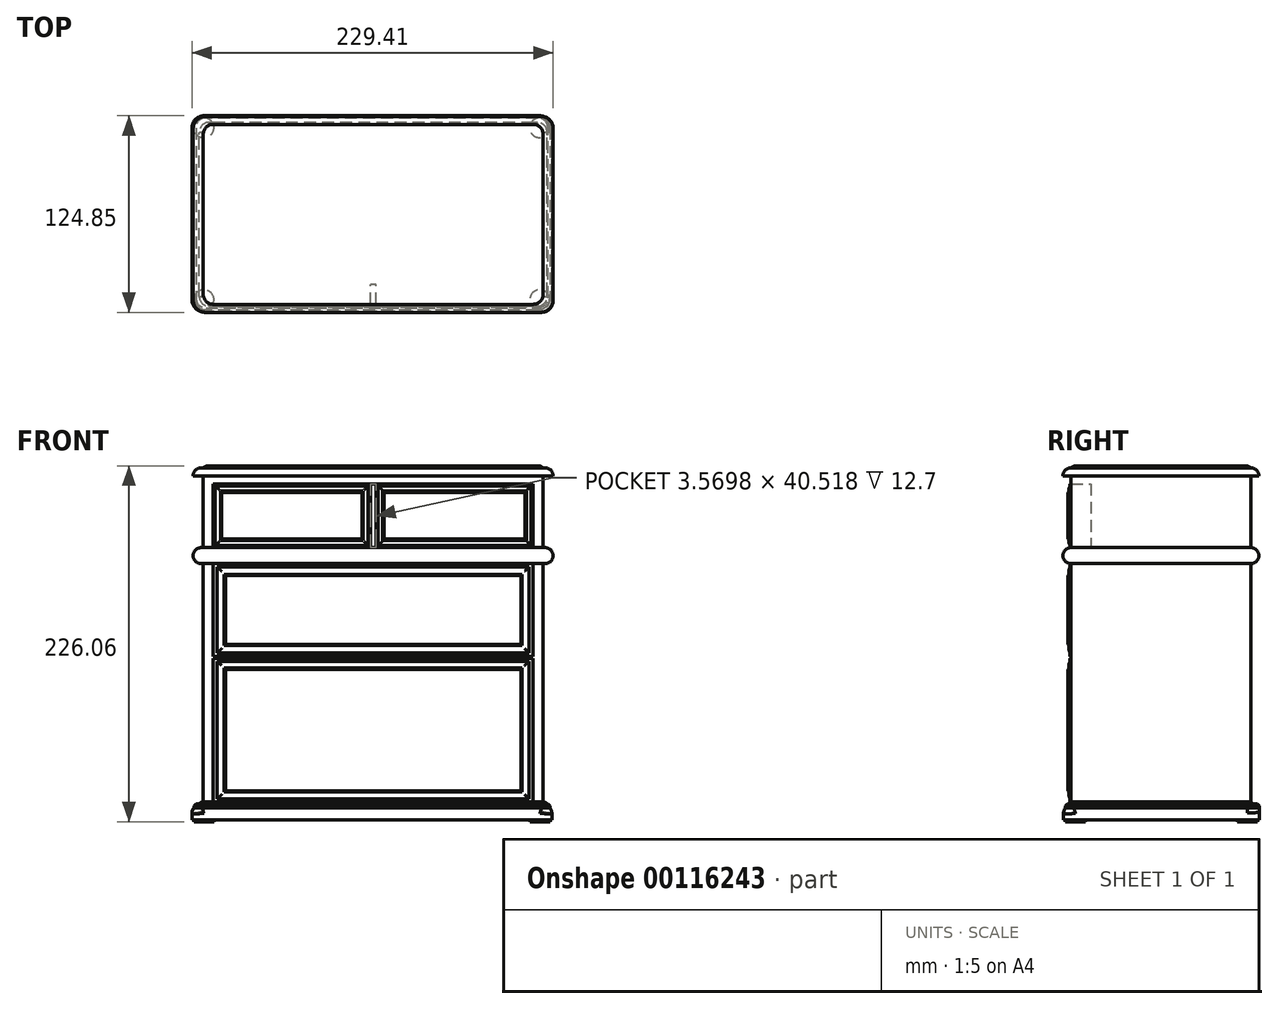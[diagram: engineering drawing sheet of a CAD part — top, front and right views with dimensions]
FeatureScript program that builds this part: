
annotation { "Feature Type Name" : "Feature", "Feature Type Description" : "" }
export const myFeature = defineFeature(function(context is Context, id is Id, definition is map)
    precondition{}
    {
        {
            var Q0;
            Q0=qCreatedBy(makeId("Top.planeOp"),FACE);
            var sketch = newSketch(context, id + "F0", { "sketchPlane" : qUnion([Q0])});
            skLineSegment(sketch, "E0.bottom", {"start": v(101.6, 57.15) * mm, "end": v(-101.6, 57.15) * mm});
            skLineSegment(sketch, "E0.top", {"start": v(101.6, -57.15) * mm, "end": v(-101.6, -57.15) * mm});
            skLineSegment(sketch, "E0.left", {"start": v(107.95, 50.8) * mm, "end": v(107.95, -50.8) * mm});
            skLineSegment(sketch, "E0.right", {"start": v(-107.95, 50.8) * mm, "end": v(-107.95, -50.8) * mm});
            skPoint(sketch, "E0.middle", {"position": v(0, 0) * mm});
            skPoint(sketch, "E1.visualSharp", {"position": v(-107.95, -57.15) * mm});
            skArc(sketch, "E1.filletArc", {"start": v(-107.95, -50.8) * mm, "mid": v(-106.1, -55.3) * mm, "end": v(-101.6, -57.15) * mm});
            skPoint(sketch, "E2.visualSharp", {"position": v(-107.95, 57.15) * mm});
            skArc(sketch, "E2.filletArc", {"start": v(-101.6, 57.15) * mm, "mid": v(-106.1, 55.3) * mm, "end": v(-107.95, 50.8) * mm});
            skPoint(sketch, "E3.visualSharp", {"position": v(107.95, 57.15) * mm});
            skArc(sketch, "E3.filletArc", {"start": v(107.95, 50.8) * mm, "mid": v(106.1, 55.3) * mm, "end": v(101.6, 57.15) * mm});
            skPoint(sketch, "E4.visualSharp", {"position": v(107.95, -57.15) * mm});
            skArc(sketch, "E4.filletArc", {"start": v(101.6, -57.15) * mm, "mid": v(106.1, -55.3) * mm, "end": v(107.95, -50.8) * mm});
            skSolve(sketch);
        }
        {
            var Q0;
            Q0 = qSketchRegion(id + "F0", true);
            extrude(context, id + "F1", {"entities" : qUnion([Q0]), "depth" : 1.27 * mm});
        }
        {
            var Q0;
            Q0=makeQuery(id+"F1.opExtrude","CAP_FACE",FACE,{"disambiguationData":[OSD([sQuery(id+"F0.wireOp",EDGE,"E0.bottom"),sQuery(id+"F0.wireOp",EDGE,"E0.top"),sQuery(id+"F0.wireOp",EDGE,"E0.left"),sQuery(id+"F0.wireOp",EDGE,"E0.right"),sQuery(id+"F0.wireOp",EDGE,"E1.filletArc"),sQuery(id+"F0.wireOp",EDGE,"E2.filletArc"),sQuery(id+"F0.wireOp",EDGE,"E3.filletArc"),sQuery(id+"F0.wireOp",EDGE,"E4.filletArc")])],"isStart":true});
            var sketch = newSketch(context, id + "F2", { "sketchPlane" : qUnion([Q0])});
            skLineSegment(sketch, "E5.bottom", {"start": v(106.68, 62.23) * mm, "end": v(-106.68, 62.23) * mm});
            skLineSegment(sketch, "E5.top", {"start": v(106.68, -62.23) * mm, "end": v(-106.68, -62.23) * mm});
            skLineSegment(sketch, "E5.left", {"start": v(114.3, 54.61) * mm, "end": v(114.3, -54.61) * mm});
            skLineSegment(sketch, "E5.right", {"start": v(-114.3, 54.61) * mm, "end": v(-114.3, -54.61) * mm});
            skPoint(sketch, "E5.middle", {"position": v(0, 0) * mm});
            skPoint(sketch, "E6.visualSharp", {"position": v(-114.3, -62.23) * mm});
            skArc(sketch, "E6.filletArc", {"start": v(-114.3, -54.61) * mm, "mid": v(-112.07, -60) * mm, "end": v(-106.68, -62.23) * mm});
            skPoint(sketch, "E7.visualSharp", {"position": v(-114.3, 62.23) * mm});
            skArc(sketch, "E7.filletArc", {"start": v(-106.68, 62.23) * mm, "mid": v(-112.07, 60) * mm, "end": v(-114.3, 54.61) * mm});
            skPoint(sketch, "E8.visualSharp", {"position": v(114.3, 62.23) * mm});
            skArc(sketch, "E8.filletArc", {"start": v(114.3, 54.61) * mm, "mid": v(112.07, 60) * mm, "end": v(106.68, 62.23) * mm});
            skPoint(sketch, "E9.visualSharp", {"position": v(114.3, -62.23) * mm});
            skArc(sketch, "E9.filletArc", {"start": v(106.68, -62.23) * mm, "mid": v(112.07, -60) * mm, "end": v(114.3, -54.61) * mm});
            skSolve(sketch);
        }
        {
            var Q0;
            Q0 = qSketchRegion(id + "F2", true);
            extrude(context, id + "F3", {"entities" : qUnion([Q0]), "operationType" : NewBodyOperationType.ADD, "depth" : 5.08 * mm});
        }
        {
            var Q0;
            Q0=makeQuery(id+"F3.opExtrude","CAP_FACE",FACE,{"disambiguationData":[OSD([sQuery(id+"F2.wireOp",EDGE,"E5.bottom"),sQuery(id+"F2.wireOp",EDGE,"E5.top"),sQuery(id+"F2.wireOp",EDGE,"E5.left"),sQuery(id+"F2.wireOp",EDGE,"E5.right"),sQuery(id+"F2.wireOp",EDGE,"E6.filletArc"),sQuery(id+"F2.wireOp",EDGE,"E7.filletArc"),sQuery(id+"F2.wireOp",EDGE,"E8.filletArc"),sQuery(id+"F2.wireOp",EDGE,"E9.filletArc")])],"isStart":false});
            var sketch = newSketch(context, id + "F4", { "sketchPlane" : qUnion([Q0])});
            skLineSegment(sketch, "E10.bottom", {"start": v(101.6, 57.15) * mm, "end": v(-101.6, 57.15) * mm});
            skLineSegment(sketch, "E10.top", {"start": v(101.6, -57.15) * mm, "end": v(-101.6, -57.15) * mm});
            skLineSegment(sketch, "E10.left", {"start": v(107.95, 50.8) * mm, "end": v(107.95, -50.8) * mm});
            skLineSegment(sketch, "E10.right", {"start": v(-107.95, 50.8) * mm, "end": v(-107.95, -50.8) * mm});
            skPoint(sketch, "E10.middle", {"position": v(0, 0) * mm});
            skPoint(sketch, "E11.visualSharp", {"position": v(-107.95, -57.15) * mm});
            skArc(sketch, "E11.filletArc", {"start": v(-107.95, -50.8) * mm, "mid": v(-106.1, -55.3) * mm, "end": v(-101.6, -57.15) * mm});
            skPoint(sketch, "E12.visualSharp", {"position": v(-107.95, 57.15) * mm});
            skArc(sketch, "E12.filletArc", {"start": v(-101.6, 57.15) * mm, "mid": v(-106.1, 55.3) * mm, "end": v(-107.95, 50.8) * mm});
            skPoint(sketch, "E13.visualSharp", {"position": v(107.95, 57.15) * mm});
            skArc(sketch, "E13.filletArc", {"start": v(107.95, 50.8) * mm, "mid": v(106.1, 55.3) * mm, "end": v(101.6, 57.15) * mm});
            skPoint(sketch, "E14.visualSharp", {"position": v(107.95, -57.15) * mm});
            skArc(sketch, "E14.filletArc", {"start": v(101.6, -57.15) * mm, "mid": v(106.1, -55.3) * mm, "end": v(107.95, -50.8) * mm});
            skSolve(sketch);
        }
        {
            var Q0;
            Q0 = qSketchRegion(id + "F4", true);
            extrude(context, id + "F5", {"entities" : qUnion([Q0]), "operationType" : NewBodyOperationType.ADD, "depth" : 3.8 * mm});
        }
        {
            var Q0;
            Q0=makeQuery(id+"F5.opExtrude","CAP_FACE",FACE,{"disambiguationData":[OSD([sQuery(id+"F4.wireOp",EDGE,"E10.bottom"),sQuery(id+"F4.wireOp",EDGE,"E10.top"),sQuery(id+"F4.wireOp",EDGE,"E10.left"),sQuery(id+"F4.wireOp",EDGE,"E10.right"),sQuery(id+"F4.wireOp",EDGE,"E11.filletArc"),sQuery(id+"F4.wireOp",EDGE,"E12.filletArc"),sQuery(id+"F4.wireOp",EDGE,"E13.filletArc"),sQuery(id+"F4.wireOp",EDGE,"E14.filletArc")])],"isStart":false});
            var sketch = newSketch(context, id + "F6", { "sketchPlane" : qUnion([Q0])});
            skLineSegment(sketch, "E15.bottom", {"start": v(101.6, 57.15) * mm, "end": v(-101.6, 57.15) * mm});
            skLineSegment(sketch, "E15.top", {"start": v(101.6, -57.15) * mm, "end": v(-101.6, -57.15) * mm});
            skLineSegment(sketch, "E15.left", {"start": v(107.95, 50.8) * mm, "end": v(107.95, -50.8) * mm});
            skLineSegment(sketch, "E15.right", {"start": v(-107.95, 50.8) * mm, "end": v(-107.95, -50.8) * mm});
            skPoint(sketch, "E15.middle", {"position": v(0, 0) * mm});
            skPoint(sketch, "E16.visualSharp", {"position": v(-107.95, 57.15) * mm});
            skArc(sketch, "E16.filletArc", {"start": v(-101.6, 57.15) * mm, "mid": v(-106.1, 55.3) * mm, "end": v(-107.95, 50.8) * mm});
            skPoint(sketch, "E17.visualSharp", {"position": v(-107.95, -57.15) * mm});
            skArc(sketch, "E17.filletArc", {"start": v(-107.95, -50.8) * mm, "mid": v(-106.1, -55.3) * mm, "end": v(-101.6, -57.15) * mm});
            skPoint(sketch, "E18.visualSharp", {"position": v(107.95, -57.15) * mm});
            skArc(sketch, "E18.filletArc", {"start": v(101.6, -57.15) * mm, "mid": v(106.1, -55.3) * mm, "end": v(107.95, -50.8) * mm});
            skPoint(sketch, "E19.visualSharp", {"position": v(107.95, 57.15) * mm});
            skArc(sketch, "E19.filletArc", {"start": v(107.95, 50.8) * mm, "mid": v(106.1, 55.3) * mm, "end": v(101.6, 57.15) * mm});
            skSolve(sketch);
        }
        {
            var Q0;
            Q0 = qSketchRegion(id + "F6", true);
            extrude(context, id + "F7", {"entities" : qUnion([Q0]), "operationType" : NewBodyOperationType.ADD, "depth" : 203.2 * mm});
        }
        {
            var Q0;
            Q0=makeQuery(id+"F7.opExtrude","CAP_FACE",FACE,{"disambiguationData":[OSD([sQuery(id+"F6.wireOp",EDGE,"E15.bottom"),sQuery(id+"F6.wireOp",EDGE,"E15.top"),sQuery(id+"F6.wireOp",EDGE,"E15.left"),sQuery(id+"F6.wireOp",EDGE,"E15.right"),sQuery(id+"F6.wireOp",EDGE,"E16.filletArc"),sQuery(id+"F6.wireOp",EDGE,"E17.filletArc"),sQuery(id+"F6.wireOp",EDGE,"E18.filletArc"),sQuery(id+"F6.wireOp",EDGE,"E19.filletArc")])],"isStart":false});
            var sketch = newSketch(context, id + "F8", { "sketchPlane" : qUnion([Q0])});
            skLineSegment(sketch, "E20.bottom", {"start": v(104.14, 58.42) * mm, "end": v(-104.14, 58.42) * mm});
            skLineSegment(sketch, "E20.top", {"start": v(104.14, -58.42) * mm, "end": v(-104.14, -58.42) * mm});
            skLineSegment(sketch, "E20.left", {"start": v(110.49, 52.07) * mm, "end": v(110.49, -52.07) * mm});
            skLineSegment(sketch, "E20.right", {"start": v(-110.49, 52.07) * mm, "end": v(-110.49, -52.07) * mm});
            skPoint(sketch, "E20.middle", {"position": v(0, 0) * mm});
            skPoint(sketch, "E21.visualSharp", {"position": v(-110.49, 58.42) * mm});
            skArc(sketch, "E21.filletArc", {"start": v(-104.14, 58.42) * mm, "mid": v(-108.63, 56.56) * mm, "end": v(-110.5, 52.07) * mm});
            skPoint(sketch, "E22.visualSharp", {"position": v(-110.49, -58.42) * mm});
            skArc(sketch, "E22.filletArc", {"start": v(-110.5, -52.07) * mm, "mid": v(-108.63, -56.56) * mm, "end": v(-104.14, -58.42) * mm});
            skPoint(sketch, "E23.visualSharp", {"position": v(110.49, -58.42) * mm});
            skArc(sketch, "E23.filletArc", {"start": v(104.14, -58.42) * mm, "mid": v(108.63, -56.56) * mm, "end": v(110.5, -52.07) * mm});
            skPoint(sketch, "E24.visualSharp", {"position": v(110.49, 58.42) * mm});
            skArc(sketch, "E24.filletArc", {"start": v(110.5, 52.07) * mm, "mid": v(108.63, 56.56) * mm, "end": v(104.14, 58.42) * mm});
            skSolve(sketch);
        }
        {
            var Q0;
            Q0 = qSketchRegion(id + "F8", true);
            extrude(context, id + "F9", {"entities" : qUnion([Q0]), "operationType" : NewBodyOperationType.ADD, "depth" : 1.27 * mm});
        }
        {
            var Q0;
            Q0=makeQuery(id+"F9.opExtrude","CAP_FACE",FACE,{"disambiguationData":[OSD([sQuery(id+"F8.wireOp",EDGE,"E20.bottom"),sQuery(id+"F8.wireOp",EDGE,"E20.top"),sQuery(id+"F8.wireOp",EDGE,"E20.left"),sQuery(id+"F8.wireOp",EDGE,"E20.right"),sQuery(id+"F8.wireOp",EDGE,"E21.filletArc"),sQuery(id+"F8.wireOp",EDGE,"E22.filletArc"),sQuery(id+"F8.wireOp",EDGE,"E23.filletArc"),sQuery(id+"F8.wireOp",EDGE,"E24.filletArc")])],"isStart":false});
            var sketch = newSketch(context, id + "F10", { "sketchPlane" : qUnion([Q0])});
            skLineSegment(sketch, "E25.bottom", {"start": v(104.6, 60.63) * mm, "end": v(-106.22, 60.63) * mm});
            skLineSegment(sketch, "E25.top", {"start": v(104.6, -62.56) * mm, "end": v(-106.22, -62.56) * mm});
            skLineSegment(sketch, "E25.left", {"start": v(112.22, 53) * mm, "end": v(112.22, -54.94) * mm});
            skLineSegment(sketch, "E25.right", {"start": v(-113.84, 53) * mm, "end": v(-113.84, -54.94) * mm});
            skPoint(sketch, "E25.middle", {"position": v(-0.81, -0.97) * mm});
            skPoint(sketch, "E26.visualSharp", {"position": v(-113.84, -62.56) * mm});
            skArc(sketch, "E26.filletArc", {"start": v(-113.84, -54.94) * mm, "mid": v(-111.61, -60.33) * mm, "end": v(-106.22, -62.56) * mm});
            skPoint(sketch, "E27.visualSharp", {"position": v(-113.84, 60.63) * mm});
            skArc(sketch, "E27.filletArc", {"start": v(-106.22, 60.63) * mm, "mid": v(-111.61, 58.4) * mm, "end": v(-113.84, 53) * mm});
            skPoint(sketch, "E28.visualSharp", {"position": v(112.22, 60.63) * mm});
            skArc(sketch, "E28.filletArc", {"start": v(112.22, 53) * mm, "mid": v(109.99, 58.4) * mm, "end": v(104.6, 60.63) * mm});
            skPoint(sketch, "E29.visualSharp", {"position": v(112.22, -62.56) * mm});
            skArc(sketch, "E29.filletArc", {"start": v(104.6, -62.56) * mm, "mid": v(109.99, -60.33) * mm, "end": v(112.22, -54.94) * mm});
            skSolve(sketch);
        }
        {
            var Q0;
            Q0 = qSketchRegion(id + "F10", true);
            extrude(context, id + "F11", {"entities" : qUnion([Q0]), "operationType" : NewBodyOperationType.ADD, "depth" : 2.54 * mm});
        }
        {
            var Q0;
            Q0=makeQuery(id+"F11.opExtrude","CAP_FACE",FACE,{"disambiguationData":[OSD([sQuery(id+"F10.wireOp",EDGE,"E25.bottom"),sQuery(id+"F10.wireOp",EDGE,"E25.top"),sQuery(id+"F10.wireOp",EDGE,"E25.left"),sQuery(id+"F10.wireOp",EDGE,"E25.right"),sQuery(id+"F10.wireOp",EDGE,"E26.filletArc"),sQuery(id+"F10.wireOp",EDGE,"E27.filletArc"),sQuery(id+"F10.wireOp",EDGE,"E28.filletArc"),sQuery(id+"F10.wireOp",EDGE,"E29.filletArc")])],"isStart":false});
            var sketch = newSketch(context, id + "F12", { "sketchPlane" : qUnion([Q0])});
            skLineSegment(sketch, "E30.bottom", {"start": v(105.87, 61.84) * mm, "end": v(-107.5, 61.84) * mm});
            skLineSegment(sketch, "E30.top", {"start": v(105.87, -62.62) * mm, "end": v(-107.5, -62.62) * mm});
            skLineSegment(sketch, "E30.left", {"start": v(113.49, 54.22) * mm, "end": v(113.49, -55) * mm});
            skLineSegment(sketch, "E30.right", {"start": v(-115.11, 54.22) * mm, "end": v(-115.11, -55) * mm});
            skPoint(sketch, "E30.middle", {"position": v(-0.81, -0.4) * mm});
            skPoint(sketch, "E31.visualSharp", {"position": v(-115.11, -62.62) * mm});
            skArc(sketch, "E31.filletArc", {"start": v(-115.11, -55) * mm, "mid": v(-112.88, -60.39) * mm, "end": v(-107.5, -62.62) * mm});
            skPoint(sketch, "E32.visualSharp", {"position": v(-115.11, 61.84) * mm});
            skArc(sketch, "E32.filletArc", {"start": v(-107.5, 61.84) * mm, "mid": v(-112.88, 59.6) * mm, "end": v(-115.11, 54.22) * mm});
            skPoint(sketch, "E33.visualSharp", {"position": v(113.49, 61.84) * mm});
            skArc(sketch, "E33.filletArc", {"start": v(113.49, 54.22) * mm, "mid": v(111.26, 59.6) * mm, "end": v(105.87, 61.84) * mm});
            skPoint(sketch, "E34.visualSharp", {"position": v(113.49, -62.62) * mm});
            skArc(sketch, "E34.filletArc", {"start": v(105.87, -62.62) * mm, "mid": v(111.26, -60.39) * mm, "end": v(113.49, -55) * mm});
            skSolve(sketch);
        }
        {
            var Q0;
            Q0 = qSketchRegion(id + "F12", true);
            extrude(context, id + "F13", {"entities" : qUnion([Q0]), "operationType" : NewBodyOperationType.ADD, "depth" : 7.62 * mm});
        }
        {
            var Q0;
            Q0=makeQuery(id+"F9.opExtrude","CAP_EDGE",EDGE,{"disambiguationData":[OSD([sQuery(id+"F8.wireOp",EDGE,"E20.bottom")])],"isStart":true});
            var Q1;
            Q1=makeQuery(id+"F13.opExtrude","CAP_EDGE",EDGE,{"disambiguationData":[OSD([sQuery(id+"F12.wireOp",EDGE,"E30.bottom")])],"isStart":true});
            fillet(context, id + "F14", {"entities" : qUnion([Q0, Q1]), "radius" : 5.08 * mm, "tangentPropagation" : true, "allowEdgeOverflow" : false});
        }
        {
            var Q0;
            Q0=makeQuery(id+"F11.opExtrude","CAP_EDGE",EDGE,{"disambiguationData":[OSD([sQuery(id+"F10.wireOp",EDGE,"E25.bottom")])],"isStart":true});
            chamfer(context, id + "F15", {"entities" : qUnion([Q0]), "width" : 1.27 * mm, "tangentPropagation" : true});
        }
        {
            var Q0;
            Q0=makeQuery(id+"F1.opExtrude","CAP_EDGE",EDGE,{"disambiguationData":[OSD([sQuery(id+"F0.wireOp",EDGE,"E0.top")])],"isStart":false});
            var Q1;
            Q1=makeQuery(id+"F5.opExtrude","CAP_EDGE",EDGE,{"disambiguationData":[OSD([sQuery(id+"F4.wireOp",EDGE,"E10.bottom")])],"isStart":true});
            fillet(context, id + "F16", {"entities" : qUnion([Q0, Q1]), "radius" : 5.08 * mm, "tangentPropagation" : true, "allowEdgeOverflow" : false});
        }
        {
            var Q0;
            Q0=makeQuery(id+"F3.opExtrude","CAP_EDGE",EDGE,{"disambiguationData":[OSD([sQuery(id+"F2.wireOp",EDGE,"E5.bottom")])],"isStart":true});
            fillet(context, id + "F17", {"entities" : qUnion([Q0]), "radius" : 5.08 * mm, "tangentPropagation" : true, "allowEdgeOverflow" : false});
        }
        {
            var Q0;
            Q0=makeQuery(id+"F13.opExtrude","CAP_FACE",FACE,{"disambiguationData":[OSD([sQuery(id+"F12.wireOp",EDGE,"E30.bottom"),sQuery(id+"F12.wireOp",EDGE,"E30.top"),sQuery(id+"F12.wireOp",EDGE,"E30.left"),sQuery(id+"F12.wireOp",EDGE,"E30.right"),sQuery(id+"F12.wireOp",EDGE,"E31.filletArc"),sQuery(id+"F12.wireOp",EDGE,"E32.filletArc"),sQuery(id+"F12.wireOp",EDGE,"E33.filletArc"),sQuery(id+"F12.wireOp",EDGE,"E34.filletArc")])],"isStart":false});
            var sketch = newSketch(context, id + "F18", { "sketchPlane" : qUnion([Q0])});
            skCircle(sketch, "E35", {"center": v(-107.5, -55) * mm, "radius": 6.35 * mm});
            skCircle(sketch, "E36", {"center": v(-107.5, 54.22) * mm, "radius": 6.35 * mm});
            skCircle(sketch, "E37", {"center": v(105.87, 54.22) * mm, "radius": 6.35 * mm});
            skCircle(sketch, "E38", {"center": v(105.87, -55) * mm, "radius": 6.35 * mm});
            skSolve(sketch);
        }
        {
            var Q0;
            Q0 = qSketchRegion(id + "F18", true);
            extrude(context, id + "F19", {"entities" : qUnion([Q0]), "operationType" : NewBodyOperationType.ADD, "depth" : 1.27 * mm});
        }
        {
            var Q0;
            Q0=makeQuery(id+"F7.boolean.opBoolean","MERGE",FACE,{"derivedFrom":[makeQuery(id+"F5.opExtrude","SWEPT_FACE",FACE,{"disambiguationData":[OSD([sQuery(id+"F4.wireOp",EDGE,"E10.bottom")])]}),makeQuery(id+"F7.opExtrude","SWEPT_FACE",FACE,{"disambiguationData":[OSD([sQuery(id+"F6.wireOp",EDGE,"E15.bottom")])]})]});
            var sketch = newSketch(context, id + "F20", { "sketchPlane" : qUnion([Q0])});
            skPoint(sketch, "E39.0", {"position": v(-101.6, -10.16) * mm});
            skPoint(sketch, "E40.0", {"position": v(101.6, -10.16) * mm});
            skPoint(sketch, "E41.0", {"position": v(101.6, -212.1) * mm});
            skPoint(sketch, "E42.0", {"position": v(-101.6, -212.1) * mm});
            skLineSegment(sketch, "E43", {"start": v(-101.6, -212.1) * mm, "end": v(-101.6, -121) * mm});
            skLineSegment(sketch, "E44", {"start": v(-101.6, -119.67) * mm, "end": v(-101.6, -60.84) * mm});
            skLineSegment(sketch, "E45", {"start": v(-101.6, -60.84) * mm, "end": v(101.6, -60.84) * mm});
            skLineSegment(sketch, "E46", {"start": v(101.6, -60.84) * mm, "end": v(101.6, -119.67) * mm});
            skLineSegment(sketch, "E47", {"start": v(101.6, -119.67) * mm, "end": v(-101.6, -119.67) * mm});
            skLineSegment(sketch, "E48", {"start": v(0, -10.16) * mm, "end": v(0, -50.68) * mm});
            skPoint(sketch, "E48.endSnap0", {"position": v(0, -10.16) * mm});
            skLineSegment(sketch, "E49", {"start": v(-0.53, -50.68) * mm, "end": v(-101.6, -50.68) * mm});
            skLineSegment(sketch, "E50", {"start": v(-101.6, -50.68) * mm, "end": v(-101.6, -10.16) * mm});
            skLineSegment(sketch, "E51", {"start": v(-101.6, -10.16) * mm, "end": v(-0.53, -10.16) * mm});
            skLineSegment(sketch, "E52", {"start": v(0.53, -50.68) * mm, "end": v(101.6, -50.68) * mm});
            skLineSegment(sketch, "E53", {"start": v(101.6, -50.68) * mm, "end": v(101.6, -10.16) * mm});
            skLineSegment(sketch, "E54", {"start": v(0.53, -10.16) * mm, "end": v(101.6, -10.16) * mm});
            skLineSegment(sketch, "E55", {"start": v(-0.53, -50.68) * mm, "end": v(-0.53, -10.16) * mm});
            skLineSegment(sketch, "E56", {"start": v(0.53, -50.68) * mm, "end": v(0.53, -10.16) * mm});
            skLineSegment(sketch, "E57.bottom", {"start": v(-101.6, -121) * mm, "end": v(101.6, -121) * mm});
            skLineSegment(sketch, "E57.top", {"start": v(-101.6, -212.1) * mm, "end": v(101.6, -212.1) * mm});
            skLineSegment(sketch, "E57.left", {"start": v(-101.6, -121) * mm, "end": v(-101.6, -212.1) * mm});
            skLineSegment(sketch, "E57.right", {"start": v(101.6, -121) * mm, "end": v(101.6, -212.1) * mm});
            skLineSegment(sketch, "E58", {"start": v(-0.53, -50.68) * mm, "end": v(0, -50.68) * mm});
            skLineSegment(sketch, "E59", {"start": v(0, -50.68) * mm, "end": v(0.53, -50.68) * mm});
            skLineSegment(sketch, "E60", {"start": v(-101.6, -50.68) * mm, "end": v(-101.6, -60.84) * mm});
            skLineSegment(sketch, "E61", {"start": v(101.6, -50.68) * mm, "end": v(101.6, -60.84) * mm});
            skLineSegment(sketch, "E62", {"start": v(-0.53, -10.16) * mm, "end": v(0, -10.16) * mm});
            skLineSegment(sketch, "E63", {"start": v(0, -10.16) * mm, "end": v(0.53, -10.16) * mm});
            skSolve(sketch);
        }
        {
            var Q0;
            Q0=sQuery(id+"F2.wireOp",EDGE,"E5.top");
            var Q1;
            {var subQ0=sQuery(id+"F0.wireOp",EDGE,"E0.bottom");Q1=makeQuery(id+"F16.opFillet","BLEND_EDGE",EDGE,{"blendedFrom":[makeQuery(id+"F1.opExtrude","CAP_EDGE",EDGE,{"disambiguationData":[OSD([subQ0])],"isStart":false}),makeQuery(id+"F1.opExtrude","CAP_FACE",FACE,{"disambiguationData":[OSD([subQ0,sQuery(id+"F0.wireOp",EDGE,"E0.top"),sQuery(id+"F0.wireOp",EDGE,"E0.left"),sQuery(id+"F0.wireOp",EDGE,"E0.right"),sQuery(id+"F0.wireOp",EDGE,"E1.filletArc"),sQuery(id+"F0.wireOp",EDGE,"E2.filletArc"),sQuery(id+"F0.wireOp",EDGE,"E3.filletArc"),sQuery(id+"F0.wireOp",EDGE,"E4.filletArc")])],"isStart":false})],"blendedInto":[makeQuery(id+"F1.opExtrude","CAP_FACE",FACE,{"disambiguationData":[OSD([subQ0,sQuery(id+"F0.wireOp",EDGE,"E0.top"),sQuery(id+"F0.wireOp",EDGE,"E0.left"),sQuery(id+"F0.wireOp",EDGE,"E0.right"),sQuery(id+"F0.wireOp",EDGE,"E1.filletArc"),sQuery(id+"F0.wireOp",EDGE,"E2.filletArc"),sQuery(id+"F0.wireOp",EDGE,"E3.filletArc"),sQuery(id+"F0.wireOp",EDGE,"E4.filletArc")])],"isStart":false})]});}
            revolve(context, id + "F21", {"bodyType" : ToolBodyType.SURFACE, "operationType" : NewBodyOperationType.INTERSECT, "surfaceEntities" : qUnion([Q0]), "axis" : qUnion([Q1]), "revolveType" : RevolveType.FULL});
        }
        {
            var Q0;
            Q0=makeQuery(id+"F20.imprint","IMPRINT",FACE,{"disambiguationData":[TD([[makeQuery(id+"F20.imprint","IMPRINT",EDGE,{"derivedFrom":sQuery(id+"F20.wireOp",EDGE,"E49")}),-1.0]])]});
            var Q1;
            Q1=makeQuery(id+"F20.imprint","IMPRINT",FACE,{"disambiguationData":[TD([[makeQuery(id+"F20.imprint","IMPRINT",EDGE,{"derivedFrom":sQuery(id+"F20.wireOp",EDGE,"E52")}),1.0]])]});
            var Q2;
            Q2=makeQuery(id+"F20.imprint","IMPRINT",FACE,{"disambiguationData":[TD([[makeQuery(id+"F20.imprint","IMPRINT",EDGE,{"derivedFrom":sQuery(id+"F20.wireOp",EDGE,"E44")}),-1.0]])]});
            var Q3;
            Q3=makeQuery(id+"F20.imprint","IMPRINT",FACE,{"disambiguationData":[TD([[makeQuery(id+"F20.imprint","IMPRINT",EDGE,{"derivedFrom":sQuery(id+"F20.wireOp",EDGE,"E57.bottom")}),-1.0]])]});
            var Q4;
            Q4=makeQuery(id+"F20.imprint","IMPRINT",FACE,{"disambiguationData":[TD([[makeQuery(id+"F20.imprint","IMPRINT",EDGE,{"derivedFrom":sQuery(id+"F20.wireOp",EDGE,"E48")}),1.0]])]});
            var Q5;
            Q5=makeQuery(id+"F20.imprint","IMPRINT",FACE,{"disambiguationData":[TD([[makeQuery(id+"F20.imprint","IMPRINT",EDGE,{"derivedFrom":sQuery(id+"F20.wireOp",EDGE,"E48")}),-1.0]])]});
            extrude(context, id + "F22", {"entities" : qUnion([Q0, Q1, Q2, Q3, Q4, Q5]), "operationType" : NewBodyOperationType.REMOVE, "oppositeDirection" : true, "depth" : 12.7 * mm});
        }
        {
            var Q0;
            Q0=makeQuery(id+"F20.imprint","IMPRINT",FACE,{"disambiguationData":[TD([[makeQuery(id+"F20.imprint","IMPRINT",EDGE,{"derivedFrom":sQuery(id+"F20.wireOp",EDGE,"E45")}),1.0]])]});
            extrude(context, id + "F23", {"entities" : qUnion([Q0]), "operationType" : NewBodyOperationType.ADD, "depth" : 5.08 * mm});
        }
        {
            var Q0;
            {var subQ0=sQuery(id+"F20.wireOp",EDGE,"E45");Q0=makeQuery(id+"F23.boolean.opBoolean","MERGE",FACE,{"derivedFrom":[makeQuery(id+"F22.boolean.opBoolean","COPY",FACE,{"derivedFrom":makeQuery(id+"F22.opExtrude","SWEPT_FACE",FACE,{"disambiguationData":[OSD([subQ0])]})}),makeQuery(id+"F23.opExtrude","SWEPT_FACE",FACE,{"disambiguationData":[OSD([subQ0])]})]});}
            var sketch = newSketch(context, id + "F24", { "sketchPlane" : qUnion([Q0])});
            skLineSegment(sketch, "E64.0", {"start": v(114.3, 54.61) * mm, "end": v(114.3, -54.61) * mm});
            skArc(sketch, "E65.0", {"start": v(106.68, -62.23) * mm, "mid": v(112.07, -60) * mm, "end": v(114.3, -54.61) * mm});
            skLineSegment(sketch, "E66.0", {"start": v(106.68, -62.23) * mm, "end": v(-106.68, -62.23) * mm});
            skArc(sketch, "E67.0", {"start": v(-114.3, -54.61) * mm, "mid": v(-112.07, -60) * mm, "end": v(-106.68, -62.23) * mm});
            skLineSegment(sketch, "E68.0", {"start": v(-114.3, 54.61) * mm, "end": v(-114.3, -54.61) * mm});
            skArc(sketch, "E69.0", {"start": v(-106.68, 62.23) * mm, "mid": v(-112.07, 60) * mm, "end": v(-114.3, 54.61) * mm});
            skLineSegment(sketch, "E70.0", {"start": v(106.68, 62.23) * mm, "end": v(-106.68, 62.23) * mm});
            skArc(sketch, "E71.0", {"start": v(114.3, 54.61) * mm, "mid": v(112.07, 60) * mm, "end": v(106.68, 62.23) * mm});
            skSolve(sketch);
        }
        {
            var Q0;
            Q0 = qSketchRegion(id + "F24", true);
            extrude(context, id + "F25", {"entities" : qUnion([Q0]), "operationType" : NewBodyOperationType.ADD, "oppositeDirection" : true, "depth" : 10.16 * mm});
        }
        {
            var Q0;
            Q0=makeQuery(id+"F25.boolean.opBoolean","MERGE",EDGE,{"derivedFrom":[makeQuery(id+"F23.opExtrude","CAP_EDGE",EDGE,{"disambiguationData":[OSD([sQuery(id+"F20.wireOp",EDGE,"E49"),sQuery(id+"F20.wireOp",EDGE,"E52"),sQuery(id+"F20.wireOp",EDGE,"E58"),sQuery(id+"F20.wireOp",EDGE,"E59")])],"isStart":false}),makeQuery(id+"F25.opExtrude","CAP_EDGE",EDGE,{"disambiguationData":[OSD([sQuery(id+"F24.wireOp",EDGE,"E70.0")])],"isStart":false})]});
            var Q1;
            Q1=makeQuery(id+"F25.boolean.opBoolean","MERGE",EDGE,{"derivedFrom":[makeQuery(id+"F23.opExtrude","CAP_EDGE",EDGE,{"disambiguationData":[OSD([sQuery(id+"F20.wireOp",EDGE,"E45")])],"isStart":false}),makeQuery(id+"F25.opExtrude","CAP_EDGE",EDGE,{"disambiguationData":[OSD([sQuery(id+"F24.wireOp",EDGE,"E70.0")])],"isStart":true})]});
            fillet(context, id + "F26", {"entities" : qUnion([Q0, Q1]), "radius" : 5.08 * mm, "tangentPropagation" : true, "allowEdgeOverflow" : false});
        }
        {
            var Q0;
            Q0=makeQuery(id+"F22.boolean.opBoolean","COPY",FACE,{"derivedFrom":makeQuery(id+"F22.opExtrude","CAP_FACE",FACE,{"disambiguationData":[OSD([sQuery(id+"F20.wireOp",EDGE,"E57.bottom"),sQuery(id+"F20.wireOp",EDGE,"E57.top"),sQuery(id+"F20.wireOp",EDGE,"E57.left"),sQuery(id+"F20.wireOp",EDGE,"E57.right")])],"isStart":false})});
            var sketch = newSketch(context, id + "F27", { "sketchPlane" : qUnion([Q0])});
            skLineSegment(sketch, "E72.0", {"start": v(-101.6, -212.1) * mm, "end": v(-101.6, -121) * mm});
            skLineSegment(sketch, "E73.0", {"start": v(-101.6, -121) * mm, "end": v(101.6, -121) * mm});
            skLineSegment(sketch, "E74.0", {"start": v(101.6, -212.1) * mm, "end": v(-101.6, -212.1) * mm});
            skLineSegment(sketch, "E75.0", {"start": v(101.6, -212.1) * mm, "end": v(101.6, -121) * mm});
            skLineSegment(sketch, "E76.0.0", {"start": v(101.6, -60.84) * mm, "end": v(-101.6, -60.84) * mm});
            skLineSegment(sketch, "E76.0.1", {"start": v(-101.6, -60.84) * mm, "end": v(-101.6, -119.67) * mm});
            skLineSegment(sketch, "E76.0.2", {"start": v(-101.6, -119.67) * mm, "end": v(101.6, -119.67) * mm});
            skLineSegment(sketch, "E76.0.3", {"start": v(101.6, -119.67) * mm, "end": v(101.6, -60.84) * mm});
            skPoint(sketch, "E77", {"position": v(-101.6, -166.55) * mm});
            skPoint(sketch, "E78", {"position": v(0, -121) * mm});
            skLineSegment(sketch, "E79", {"start": v(-101.6, -166.55) * mm, "end": v(95.09, -166.55) * mm, "construction": true});
            skLineSegment(sketch, "E80", {"start": v(0, -121) * mm, "end": v(0, -166.55) * mm, "construction": true});
            skPoint(sketch, "E80.endSnap0", {"position": v(-3.26, -166.55) * mm});
            skLineSegment(sketch, "E81.bottom", {"start": v(98.96, -122.85) * mm, "end": v(-98.96, -122.85) * mm});
            skLineSegment(sketch, "E81.top", {"start": v(98.96, -210.25) * mm, "end": v(-98.96, -210.25) * mm});
            skLineSegment(sketch, "E81.left", {"start": v(98.96, -122.85) * mm, "end": v(98.96, -210.25) * mm});
            skLineSegment(sketch, "E81.right", {"start": v(-98.96, -122.85) * mm, "end": v(-98.96, -210.25) * mm});
            skPoint(sketch, "E81.middle", {"position": v(0, -166.55) * mm});
            skLineSegment(sketch, "E82.bottom", {"start": v(96.3, -125.38) * mm, "end": v(-96.3, -125.38) * mm});
            skLineSegment(sketch, "E82.top", {"start": v(96.3, -207.72) * mm, "end": v(-96.3, -207.72) * mm});
            skLineSegment(sketch, "E82.left", {"start": v(96.3, -125.38) * mm, "end": v(96.3, -207.72) * mm});
            skLineSegment(sketch, "E82.right", {"start": v(-96.3, -125.38) * mm, "end": v(-96.3, -207.72) * mm});
            skPoint(sketch, "E83", {"position": v(-101.6, -90.25) * mm});
            skPoint(sketch, "E84", {"position": v(0, -60.84) * mm});
            skLineSegment(sketch, "E85", {"start": v(-101.6, -90.25) * mm, "end": v(86.76, -90.25) * mm, "construction": true});
            skLineSegment(sketch, "E86", {"start": v(0, -60.84) * mm, "end": v(0, -90.25) * mm, "construction": true});
            skLineSegment(sketch, "E87.bottom", {"start": v(98.96, -62.98) * mm, "end": v(-98.96, -62.98) * mm});
            skLineSegment(sketch, "E87.top", {"start": v(98.96, -117.53) * mm, "end": v(-98.96, -117.53) * mm});
            skLineSegment(sketch, "E87.left", {"start": v(98.96, -62.98) * mm, "end": v(98.96, -117.53) * mm});
            skLineSegment(sketch, "E87.right", {"start": v(-98.96, -62.98) * mm, "end": v(-98.96, -117.53) * mm});
            skPoint(sketch, "E87.middle", {"position": v(0, -90.25) * mm});
            skLineSegment(sketch, "E88.bottom", {"start": v(96.3, -65.9) * mm, "end": v(-96.3, -65.9) * mm});
            skLineSegment(sketch, "E88.top", {"start": v(96.3, -114.61) * mm, "end": v(-96.3, -114.61) * mm});
            skLineSegment(sketch, "E88.left", {"start": v(96.3, -65.9) * mm, "end": v(96.3, -114.61) * mm});
            skLineSegment(sketch, "E88.right", {"start": v(-96.3, -65.9) * mm, "end": v(-96.3, -114.61) * mm});
            skLineSegment(sketch, "E89", {"start": v(0, -60.84) * mm, "end": v(0, -50.68) * mm, "construction": true});
            skPoint(sketch, "E90", {"position": v(0, -30.42) * mm});
            skLineSegment(sketch, "E91.trimOffspring", {"start": v(0, -10.16) * mm, "end": v(0, 0) * mm, "construction": true});
            skPoint(sketch, "E92", {"position": v(-51.7, -30.42) * mm});
            skPoint(sketch, "E93.0", {"position": v(-101.6, -10.16) * mm});
            skPoint(sketch, "E94.0", {"position": v(101.6, -50.68) * mm});
            skLineSegment(sketch, "E95.right", {"start": v(-1.78, -10.16) * mm, "end": v(-1.78, -50.68) * mm});
            skLineSegment(sketch, "E96.right", {"start": v(0, -50.68) * mm, "end": v(0, -10.16) * mm});
            skLineSegment(sketch, "E97", {"start": v(1.78, -10.16) * mm, "end": v(1.78, -50.68) * mm});
            skLineSegment(sketch, "E98", {"start": v(-1.78, -10.16) * mm, "end": v(0, -10.16) * mm});
            skLineSegment(sketch, "E99", {"start": v(1.78, -10.16) * mm, "end": v(0, -10.16) * mm});
            skLineSegment(sketch, "E100", {"start": v(-1.78, -50.68) * mm, "end": v(0, -50.68) * mm});
            skLineSegment(sketch, "E101", {"start": v(0, -50.68) * mm, "end": v(1.78, -50.68) * mm});
            skPoint(sketch, "E102.endSnap0", {"position": v(-1.78, -30.42) * mm});
            skPoint(sketch, "E103", {"position": v(51.7, -30.42) * mm});
            skLineSegment(sketch, "E104.bottom", {"start": v(101.6, -50.68) * mm, "end": v(1.78, -50.68) * mm});
            skLineSegment(sketch, "E104.top", {"start": v(101.6, -10.16) * mm, "end": v(1.78, -10.16) * mm});
            skLineSegment(sketch, "E104.left", {"start": v(101.6, -50.68) * mm, "end": v(101.6, -10.16) * mm});
            skLineSegment(sketch, "E104.right", {"start": v(1.78, -50.68) * mm, "end": v(1.78, -10.16) * mm});
            skLineSegment(sketch, "E105.bottom", {"start": v(-1.78, -50.68) * mm, "end": v(-101.6, -50.68) * mm});
            skLineSegment(sketch, "E105.top", {"start": v(-1.78, -10.16) * mm, "end": v(-101.6, -10.16) * mm});
            skLineSegment(sketch, "E105.left", {"start": v(-1.78, -50.68) * mm, "end": v(-1.78, -10.16) * mm});
            skLineSegment(sketch, "E105.right", {"start": v(-101.6, -50.68) * mm, "end": v(-101.6, -10.16) * mm});
            skLineSegment(sketch, "E106.bottom", {"start": v(-3.1, -49.43) * mm, "end": v(-100.28, -49.43) * mm});
            skLineSegment(sketch, "E106.top", {"start": v(-3.1, -11.4) * mm, "end": v(-100.28, -11.4) * mm});
            skLineSegment(sketch, "E106.left", {"start": v(-3.1, -49.43) * mm, "end": v(-3.1, -11.4) * mm});
            skLineSegment(sketch, "E106.right", {"start": v(-100.28, -49.43) * mm, "end": v(-100.28, -11.4) * mm});
            skLineSegment(sketch, "E107.bottom", {"start": v(-4.56, -13) * mm, "end": v(-98.83, -13) * mm});
            skLineSegment(sketch, "E107.top", {"start": v(-4.56, -47.83) * mm, "end": v(-98.83, -47.83) * mm});
            skLineSegment(sketch, "E107.left", {"start": v(-4.56, -13) * mm, "end": v(-4.56, -47.83) * mm});
            skLineSegment(sketch, "E107.right", {"start": v(-98.83, -13) * mm, "end": v(-98.83, -47.83) * mm});
            skLineSegment(sketch, "E108.bottom", {"start": v(100.28, -49.43) * mm, "end": v(3.1, -49.43) * mm});
            skLineSegment(sketch, "E108.top", {"start": v(100.28, -11.4) * mm, "end": v(3.1, -11.4) * mm});
            skLineSegment(sketch, "E108.left", {"start": v(100.28, -49.43) * mm, "end": v(100.28, -11.4) * mm});
            skLineSegment(sketch, "E108.right", {"start": v(3.1, -49.43) * mm, "end": v(3.1, -11.4) * mm});
            skLineSegment(sketch, "E109.bottom", {"start": v(99.14, -47.83) * mm, "end": v(4.24, -47.83) * mm});
            skLineSegment(sketch, "E109.top", {"start": v(99.14, -13) * mm, "end": v(4.24, -13) * mm});
            skLineSegment(sketch, "E109.left", {"start": v(99.14, -47.83) * mm, "end": v(99.14, -13) * mm});
            skLineSegment(sketch, "E109.right", {"start": v(4.24, -47.83) * mm, "end": v(4.24, -13) * mm});
            skSolve(sketch);
        }
        {
            var Q0;
            Q0=makeQuery(id+"F27.imprint","IMPRINT",FACE,{"disambiguationData":[TD([[makeQuery(id+"F27.imprint","IMPRINT",EDGE,{"derivedFrom":sQuery(id+"F27.wireOp",EDGE,"E72.0")}),-1.0]])]});
            var Q1;
            Q1=makeQuery(id+"F27.imprint","IMPRINT",FACE,{"disambiguationData":[TD([[makeQuery(id+"F27.imprint","IMPRINT",EDGE,{"derivedFrom":sQuery(id+"F27.wireOp",EDGE,"E76.0.0")}),1.0]])]});
            var Q2;
            Q2=makeQuery(id+"F27.imprint","IMPRINT",FACE,{"disambiguationData":[TD([[makeQuery(id+"F27.imprint","IMPRINT",EDGE,{"derivedFrom":sQuery(id+"F27.wireOp",EDGE,"E104.bottom")}),-1.0]])]});
            var Q3;
            Q3=makeQuery(id+"F27.imprint","IMPRINT",FACE,{"disambiguationData":[TD([[makeQuery(id+"F27.imprint","IMPRINT",EDGE,{"derivedFrom":sQuery(id+"F27.wireOp",EDGE,"E105.bottom")}),-1.0]])]});
            extrude(context, id + "F28", {"entities" : qUnion([Q0, Q1, Q2, Q3]), "operationType" : NewBodyOperationType.ADD, "depth" : 13.2 * mm});
        }
        {
            var Q0;
            Q0=makeQuery(id+"F27.imprint","IMPRINT",FACE,{"disambiguationData":[TD([[makeQuery(id+"F27.imprint","IMPRINT",EDGE,{"derivedFrom":sQuery(id+"F27.wireOp",EDGE,"E81.bottom")}),1.0]])]});
            var Q1;
            Q1=makeQuery(id+"F27.imprint","IMPRINT",FACE,{"disambiguationData":[TD([[makeQuery(id+"F27.imprint","IMPRINT",EDGE,{"derivedFrom":sQuery(id+"F27.wireOp",EDGE,"E87.bottom")}),1.0]])]});
            var Q2;
            Q2=makeQuery(id+"F27.imprint","IMPRINT",FACE,{"disambiguationData":[TD([[makeQuery(id+"F27.imprint","IMPRINT",EDGE,{"derivedFrom":sQuery(id+"F27.wireOp",EDGE,"E108.bottom")}),-1.0]])]});
            var Q3;
            Q3=makeQuery(id+"F27.imprint","IMPRINT",FACE,{"disambiguationData":[TD([[makeQuery(id+"F27.imprint","IMPRINT",EDGE,{"derivedFrom":sQuery(id+"F27.wireOp",EDGE,"E106.bottom")}),-1.0]])]});
            extrude(context, id + "F29", {"entities" : qUnion([Q0, Q1, Q2, Q3]), "operationType" : NewBodyOperationType.ADD, "depth" : 13.97 * mm});
        }
        {
            var Q0;
            Q0=makeQuery(id+"F27.imprint","IMPRINT",FACE,{"disambiguationData":[TD([[makeQuery(id+"F27.imprint","IMPRINT",EDGE,{"derivedFrom":sQuery(id+"F27.wireOp",EDGE,"E82.bottom")}),1.0]])]});
            var Q1;
            Q1=makeQuery(id+"F27.imprint","IMPRINT",FACE,{"disambiguationData":[TD([[makeQuery(id+"F27.imprint","IMPRINT",EDGE,{"derivedFrom":sQuery(id+"F27.wireOp",EDGE,"E107.bottom")}),1.0]])]});
            var Q2;
            Q2=makeQuery(id+"F27.imprint","IMPRINT",FACE,{"disambiguationData":[TD([[makeQuery(id+"F27.imprint","IMPRINT",EDGE,{"derivedFrom":sQuery(id+"F27.wireOp",EDGE,"E109.bottom")}),-1.0]])]});
            var Q3;
            Q3=makeQuery(id+"F27.imprint","IMPRINT",FACE,{"disambiguationData":[TD([[makeQuery(id+"F27.imprint","IMPRINT",EDGE,{"derivedFrom":sQuery(id+"F27.wireOp",EDGE,"E88.bottom")}),1.0]])]});
            extrude(context, id + "F30", {"entities" : qUnion([Q0, Q1, Q2, Q3]), "operationType" : NewBodyOperationType.ADD, "depth" : 14.73 * mm});
        }
        {
            var Q0;
            Q0=makeQuery(id+"F30.opExtrude","CAP_FACE",FACE,{"disambiguationData":[OSD([sQuery(id+"F27.wireOp",EDGE,"E82.bottom"),sQuery(id+"F27.wireOp",EDGE,"E82.top"),sQuery(id+"F27.wireOp",EDGE,"E82.left"),sQuery(id+"F27.wireOp",EDGE,"E82.right")])],"isStart":false});
            var Q1;
            Q1=makeQuery(id+"F30.opExtrude","CAP_FACE",FACE,{"disambiguationData":[OSD([sQuery(id+"F27.wireOp",EDGE,"E88.bottom"),sQuery(id+"F27.wireOp",EDGE,"E88.top"),sQuery(id+"F27.wireOp",EDGE,"E88.left"),sQuery(id+"F27.wireOp",EDGE,"E88.right")])],"isStart":false});
            var Q2;
            Q2=makeQuery(id+"F30.opExtrude","CAP_FACE",FACE,{"disambiguationData":[OSD([sQuery(id+"F27.wireOp",EDGE,"E107.bottom"),sQuery(id+"F27.wireOp",EDGE,"E107.top"),sQuery(id+"F27.wireOp",EDGE,"E107.left"),sQuery(id+"F27.wireOp",EDGE,"E107.right")])],"isStart":false});
            var Q3;
            Q3=makeQuery(id+"F30.opExtrude","CAP_FACE",FACE,{"disambiguationData":[OSD([sQuery(id+"F27.wireOp",EDGE,"E109.bottom"),sQuery(id+"F27.wireOp",EDGE,"E109.top"),sQuery(id+"F27.wireOp",EDGE,"E109.left"),sQuery(id+"F27.wireOp",EDGE,"E109.right")])],"isStart":false});
            chamfer(context, id + "F31", {"entities" : qUnion([Q0, Q1, Q2, Q3]), "width" : 2.54 * mm, "tangentPropagation" : true});
        }
        {
            var Q0;
            Q0=makeQuery(id+"F29.opExtrude","CAP_EDGE",EDGE,{"disambiguationData":[OSD([sQuery(id+"F27.wireOp",EDGE,"E81.top")])],"isStart":false});
            var Q1;
            Q1=makeQuery(id+"F29.opExtrude","CAP_EDGE",EDGE,{"disambiguationData":[OSD([sQuery(id+"F27.wireOp",EDGE,"E81.bottom")])],"isStart":false});
            var Q2;
            Q2=makeQuery(id+"F29.opExtrude","CAP_EDGE",EDGE,{"disambiguationData":[OSD([sQuery(id+"F27.wireOp",EDGE,"E81.left")])],"isStart":false});
            var Q3;
            Q3=makeQuery(id+"F29.opExtrude","CAP_EDGE",EDGE,{"disambiguationData":[OSD([sQuery(id+"F27.wireOp",EDGE,"E81.right")])],"isStart":false});
            fillet(context, id + "F32", {"entities" : qUnion([Q0, Q1, Q2, Q3]), "radius" : 5.08 * mm, "tangentPropagation" : true, "allowEdgeOverflow" : false});
        }
        {
            var Q0;
            Q0=makeQuery(id+"F29.opExtrude","CAP_EDGE",EDGE,{"disambiguationData":[OSD([sQuery(id+"F27.wireOp",EDGE,"E87.top")])],"isStart":false});
            var Q1;
            Q1=makeQuery(id+"F29.opExtrude","CAP_EDGE",EDGE,{"disambiguationData":[OSD([sQuery(id+"F27.wireOp",EDGE,"E87.right")])],"isStart":false});
            var Q2;
            Q2=makeQuery(id+"F29.opExtrude","CAP_EDGE",EDGE,{"disambiguationData":[OSD([sQuery(id+"F27.wireOp",EDGE,"E87.bottom")])],"isStart":false});
            var Q3;
            Q3=makeQuery(id+"F29.opExtrude","CAP_EDGE",EDGE,{"disambiguationData":[OSD([sQuery(id+"F27.wireOp",EDGE,"E87.left")])],"isStart":false});
            fillet(context, id + "F33", {"entities" : qUnion([Q0, Q1, Q2, Q3]), "radius" : 5.08 * mm, "tangentPropagation" : true, "allowEdgeOverflow" : false});
        }
        {
            var Q0;
            Q0=makeQuery(id+"F29.opExtrude","CAP_EDGE",EDGE,{"disambiguationData":[OSD([sQuery(id+"F27.wireOp",EDGE,"E106.right")])],"isStart":false});
            var Q1;
            Q1=makeQuery(id+"F29.opExtrude","CAP_EDGE",EDGE,{"disambiguationData":[OSD([sQuery(id+"F27.wireOp",EDGE,"E106.bottom")])],"isStart":false});
            var Q2;
            Q2=makeQuery(id+"F29.opExtrude","CAP_EDGE",EDGE,{"disambiguationData":[OSD([sQuery(id+"F27.wireOp",EDGE,"E106.left")])],"isStart":false});
            var Q3;
            Q3=makeQuery(id+"F29.opExtrude","CAP_EDGE",EDGE,{"disambiguationData":[OSD([sQuery(id+"F27.wireOp",EDGE,"E106.top")])],"isStart":false});
            var Q4;
            Q4=makeQuery(id+"F29.opExtrude","CAP_EDGE",EDGE,{"disambiguationData":[OSD([sQuery(id+"F27.wireOp",EDGE,"E108.right")])],"isStart":false});
            var Q5;
            Q5=makeQuery(id+"F29.opExtrude","CAP_EDGE",EDGE,{"disambiguationData":[OSD([sQuery(id+"F27.wireOp",EDGE,"E108.bottom")])],"isStart":false});
            var Q6;
            Q6=makeQuery(id+"F29.opExtrude","CAP_EDGE",EDGE,{"disambiguationData":[OSD([sQuery(id+"F27.wireOp",EDGE,"E108.top")])],"isStart":false});
            var Q7;
            Q7=makeQuery(id+"F29.opExtrude","CAP_EDGE",EDGE,{"disambiguationData":[OSD([sQuery(id+"F27.wireOp",EDGE,"E108.left")])],"isStart":false});
            fillet(context, id + "F34", {"entities" : qUnion([Q0, Q1, Q2, Q3, Q4, Q5, Q6, Q7]), "radius" : 5.08 * mm, "tangentPropagation" : true, "allowEdgeOverflow" : false});
        }
    });
